# Revit family: SE
name_source: partatom
category: Lighting Fixtures
units: mm (PartAtom-declared; Revit-internal decimal feet)

## family parameters
Cut with Voids When Loaded = No
Host = Face
Light Source = No
OmniClass Number = 23.80.70.11.21
OmniClass Title = Emergency Lighting
Part Type = Normal
Room Calculation Point = No
Round Connector Dimension = Use Diameter
Shared = No

## types (4) — shared parameters
Apparent Load = 4 VA
Default Elevation = 48 "
Description = Exit Sign, Die-Cast Aluminum Housing
Glass = light Glass
Lamp = Long-Life LEDs
Load Classification = Lighting
Manufacturer = Dual Lighting
Model = SE Series
URL = https://www.currentlighting.com
Voltage = 120 V
Wattage Comments = 2.6 or 3.8 Watts

## per-type parameters (varying)
| type | Finish | Lens |
| SE -  White with Red Exit | Paint - White | Red Glass |
| SE -  White with Green Exit | Paint - White | Green Glass |
| SE -  Black with Red Exit | Paint - Black | Red Glass |
| SE -  Black with Green Exit | Paint - Black | Green Glass |

## geometry (parser evidence)
native form markers: Blend x2, Sweep x5
no freeform markers — native parametric forms only
